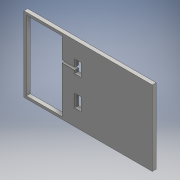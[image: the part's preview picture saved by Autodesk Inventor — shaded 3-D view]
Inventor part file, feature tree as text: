
AUTODESK INVENTOR PART (.ipt)
format: ipt  version: 2016 (Build 200138000, 138)  size: 122,880 bytes
history: native  units: mm
features: extrude x1, sketch x1
ambient origin geometry x8: Origin, YZ Plane, XZ Plane, XY Plane, X Axis, Y Axis, Z Axis, Center Point
bodies: Body1 (feature_tree)
feature tree (2):
  extrude  "Extrusion2"  Depth=59.0mm
  sketch  "Sketch1"  dims[d0=101.0mm d1=59.0mm d7=5.0mm d8=10.0mm d9=5.0mm d10=10.0mm d11=10.0mm d12=2.0mm d13=3.0mm d14=0.0mm d16=2.0mm d17=2.0mm d18=2.0mm d19=28.0mm d20=20.0mm]
